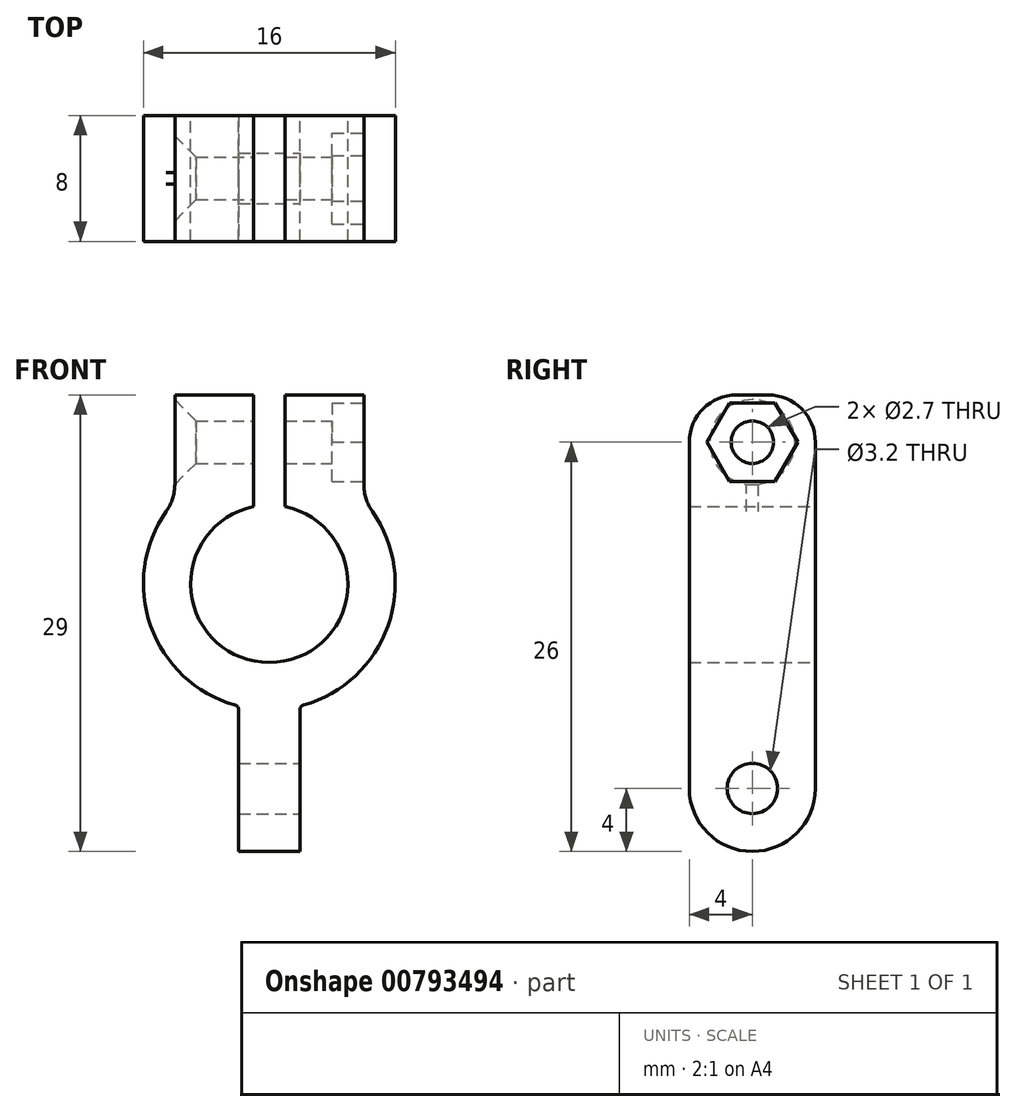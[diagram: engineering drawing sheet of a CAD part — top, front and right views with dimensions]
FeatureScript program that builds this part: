
annotation { "Feature Type Name" : "Feature", "Feature Type Description" : "" }
export const myFeature = defineFeature(function(context is Context, id is Id, definition is map)
    precondition{}
    {
        {
            var Q0;
            Q0=qCreatedBy(makeId("Front.planeOp"),FACE);
            var sketch = newSketch(context, id + "F0", { "sketchPlane" : qUnion([Q0])});
            skArc(sketch, "E0", {"start": v(-1, 4.9) * mm, "mid": v(0, -5) * mm, "end": v(1, 4.9) * mm});
            skLineSegment(sketch, "E1", {"start": v(-1, 12) * mm, "end": v(-1, 4.9) * mm});
            skLineSegment(sketch, "E2", {"start": v(1, 4.9) * mm, "end": v(1, 12) * mm});
            skLineSegment(sketch, "E3.trimOffspring", {"start": v(-1, 12) * mm, "end": v(-6, 12) * mm});
            skLineSegment(sketch, "E4", {"start": v(-1.95, -17) * mm, "end": v(-1.95, -8) * mm});
            skLineSegment(sketch, "E5", {"start": v(1.95, -8) * mm, "end": v(1.95, -17) * mm});
            skLineSegment(sketch, "E6", {"start": v(-1.95, -8) * mm, "end": v(-2.26, -8) * mm, "construction": true});
            skArc(sketch, "E7", {"start": v(-1.95, -8) * mm, "mid": v(-2.01, -7.81) * mm, "end": v(-2.18, -7.7) * mm});
            skLineSegment(sketch, "E8", {"start": v(-1.95, -17) * mm, "end": v(1.95, -17) * mm});
            skArc(sketch, "E9.MirrorCS", {"start": v(1.95, -8) * mm, "mid": v(2.01, -7.81) * mm, "end": v(2.18, -7.7) * mm});
            skLineSegment(sketch, "E10", {"start": v(-6, 12) * mm, "end": v(-6, 5.3) * mm});
            skArc(sketch, "E11", {"start": v(-2.18, -7.7) * mm, "mid": v(-7.67, -2.26) * mm, "end": v(-6, 5.3) * mm});
            skArc(sketch, "E12.MirrorCS", {"start": v(2.18, -7.7) * mm, "mid": v(7.67, -2.26) * mm, "end": v(6, 5.3) * mm});
            skLineSegment(sketch, "E13.MirrorCS", {"start": v(1, 12) * mm, "end": v(6, 12) * mm});
            skLineSegment(sketch, "E14.MirrorCS", {"start": v(6, 12) * mm, "end": v(6, 5.3) * mm});
            skSolve(sketch);
        }
        {
            var Q0;
            Q0=makeQuery(id+"F0.imprint","IMPRINT",FACE,{"disambiguationData":[TD([[makeQuery(id+"F0.imprint","IMPRINT",EDGE,{"derivedFrom":sQuery(id+"F0.wireOp",EDGE,"E0")}),-1.0]])]});
            var Q1;
            {var subQ0=sQuery(id+"F0.wireOp",EDGE,"gT4Yp9KQ-vHPQ-P8ZU-SFqX-VDEBA4EE69W3");Q1=makeQuery(id+"F0.imprint","IMPRINT",FACE,{"disambiguationData":[TD([[makeQuery(id+"F0.imprint","IMPRINT",EDGE,{"derivedFrom":subQ0}),1.0]])]});}
            extrude(context, id + "F1", {"entities" : qUnion([Q0, Q1]), "endBound" : BoundingType.SYMMETRIC, "depth" : 8 * mm, "offsetDistance" : 25 * mm});
        }
        {
            var Q0;
            Q0=makeQuery(id+"F1.opExtrude","SWEPT_FACE",FACE,{"disambiguationData":[OSD([sQuery(id+"F0.wireOp",EDGE,"E14.MirrorCS")])]});
            var sketch = newSketch(context, id + "F2", { "sketchPlane" : qUnion([Q0])});
            skCircle(sketch, "E15", {"center": v(0, 9) * mm, "radius": 1.35 * mm});
            skCircle(sketch, "E16.cCircle", {"center": v(0, 9) * mm, "radius": 2.5 * mm, "construction": true});
            skLineSegment(sketch, "E16.0", {"start": v(1.44, 11.5) * mm, "end": v(2.89, 9) * mm});
            skLineSegment(sketch, "E16.1", {"start": v(2.89, 9) * mm, "end": v(1.44, 6.5) * mm});
            skLineSegment(sketch, "E16.2", {"start": v(1.44, 6.5) * mm, "end": v(-1.44, 6.5) * mm});
            skLineSegment(sketch, "E16.3", {"start": v(-1.44, 6.5) * mm, "end": v(-2.89, 9) * mm});
            skLineSegment(sketch, "E16.4", {"start": v(-2.89, 9) * mm, "end": v(-1.44, 11.5) * mm});
            skLineSegment(sketch, "E16.5", {"start": v(-1.44, 11.5) * mm, "end": v(1.44, 11.5) * mm});
            skPoint(sketch, "E16.0.midPoint", {"position": v(2.17, 10.25) * mm});
            skSolve(sketch);
        }
        {
            var Q0;
            Q0=makeQuery(id+"F2.imprint","IMPRINT",FACE,{"disambiguationData":[TD([[makeQuery(id+"F2.imprint","IMPRINT",EDGE,{"derivedFrom":sQuery(id+"F2.wireOp",EDGE,"E15")}),1.0]])]});
            var Q1;
            {var subQ0=sQuery(id+"F2.wireOp",EDGE,"nRwaLtps-0aPM-k6Bh-PqO4-CJdIWXvHlXeP");Q1=makeQuery(id+"F2.imprint","IMPRINT",FACE,{"disambiguationData":[TD([[makeQuery(id+"F2.imprint","IMPRINT",EDGE,{"derivedFrom":subQ0}),1.0]])]});}
            var Q2;
            {var subQ0=sQuery(id+"F2.wireOp",EDGE,"26d730cf-6a02-49fb-9eb9-cb2f17dd4a160.MirrorCS");Q2=makeQuery(id+"F2.imprint","IMPRINT",FACE,{"disambiguationData":[TD([[makeQuery(id+"F2.imprint","IMPRINT",EDGE,{"derivedFrom":subQ0}),-1.0]])]});}
            extrude(context, id + "F3", {"entities" : qUnion([Q0, Q1, Q2]), "operationType" : NewBodyOperationType.REMOVE, "oppositeDirection" : true, "depth" : 25 * mm, "offsetDistance" : 25 * mm});
        }
        {
            var Q0;
            Q0=makeQuery(id+"F2.imprint","IMPRINT",FACE,{"disambiguationData":[TD([[makeQuery(id+"F2.imprint","IMPRINT",EDGE,{"derivedFrom":sQuery(id+"F2.wireOp",EDGE,"E15")}),-1.0]])]});
            extrude(context, id + "F4", {"entities" : qUnion([Q0]), "operationType" : NewBodyOperationType.REMOVE, "oppositeDirection" : true, "depth" : 2 * mm, "offsetDistance" : 25 * mm});
        }
        {
            var Q0;
            Q0=makeQuery(id+"F1.opExtrude","SWEPT_FACE",FACE,{"disambiguationData":[OSD([sQuery(id+"F0.wireOp",EDGE,"E5")])]});
            var sketch = newSketch(context, id + "F5", { "sketchPlane" : qUnion([Q0])});
            skCircle(sketch, "E17", {"center": v(0, -13) * mm, "radius": 1.6 * mm});
            skSolve(sketch);
        }
        {
            var Q0;
            Q0=makeQuery(id+"F5.imprint","IMPRINT",FACE,{"disambiguationData":[TD([[makeQuery(id+"F5.imprint","IMPRINT",EDGE,{"derivedFrom":sQuery(id+"F5.wireOp",EDGE,"E17")}),1.0]])]});
            var Q1;
            {var subQ0=sQuery(id+"F5.wireOp",EDGE,"dgfmRsRT-HZR4-KMtm-UVD4-OGYZ9sb2hiea");var subQ1=sQuery(id+"F0.wireOp",EDGE,"URoOaodK-mer2-KlBf-KcxF-PiR6j1BPeDQ6");var subQ2=makeQuery(id+"F1.opExtrude","CAP_EDGE",EDGE,{"disambiguationData":[OSD([subQ1])],"isStart":false});var subQ3=makeQuery(id+"F5.imprint","INTERSECT",VERTEX,{"derivedFrom":[subQ2,sQuery(id+"F5.wireOp",EDGE,"iwAXt04E-8AKp-sdOK-APD1-idUJ9iq6WJ0X"),subQ0]});Q1=makeQuery(id+"F5.imprint","IMPRINT",FACE,{"disambiguationData":[TD([[makeQuery(id+"F5.imprint","IMPRINT",EDGE,{"disambiguationData":[TD([[subQ3,-1.0]])],"derivedFrom":subQ0}),-1.0]])]});}
            var Q2;
            {var subQ0=sQuery(id+"F5.wireOp",EDGE,"dgfmRsRT-HZR4-KMtm-UVD4-OGYZ9sb2hiea");var subQ1=sQuery(id+"F0.wireOp",EDGE,"URoOaodK-mer2-KlBf-KcxF-PiR6j1BPeDQ6");var subQ2=makeQuery(id+"F1.opExtrude","CAP_EDGE",EDGE,{"disambiguationData":[OSD([subQ1])],"isStart":true});var subQ3=makeQuery(id+"F5.imprint","INTERSECT",VERTEX,{"derivedFrom":[subQ2,sQuery(id+"F5.wireOp",EDGE,"2524a595-133a-427d-9363-88fda697d8180.MirrorCS"),subQ0]});Q2=makeQuery(id+"F5.imprint","IMPRINT",FACE,{"disambiguationData":[TD([[makeQuery(id+"F5.imprint","IMPRINT",EDGE,{"disambiguationData":[TD([[subQ3,1.0]])],"derivedFrom":subQ0}),-1.0]])]});}
            extrude(context, id + "F6", {"entities" : qUnion([Q0, Q1, Q2]), "operationType" : NewBodyOperationType.REMOVE, "oppositeDirection" : true, "depth" : 25 * mm, "offsetDistance" : 25 * mm});
        }
        {
            var Q0;
            Q0=makeQuery(id+"F3.boolean.opBoolean","INTERSECT",EDGE,{"derivedFrom":[makeQuery(id+"F1.opExtrude","SWEPT_FACE",FACE,{"disambiguationData":[OSD([sQuery(id+"F0.wireOp",EDGE,"E10")])]}),makeQuery(id+"F3.opExtrude","SWEPT_FACE",FACE,{"disambiguationData":[OSD([sQuery(id+"F2.wireOp",EDGE,"E15")])]})]});
            chamfer(context, id + "F7", {"entities" : qUnion([Q0]), "width" : 1.35 * mm, "tangentPropagation" : true});
        }
        {
            var Q0;
            Q0=makeQuery(id+"F1.opExtrude","CAP_EDGE",EDGE,{"disambiguationData":[OSD([sQuery(id+"F0.wireOp",EDGE,"E3.trimOffspring")])],"isStart":false});
            var Q1;
            Q1=makeQuery(id+"F1.opExtrude","CAP_EDGE",EDGE,{"disambiguationData":[OSD([sQuery(id+"F0.wireOp",EDGE,"E3.trimOffspring")])],"isStart":true});
            var Q2;
            Q2=makeQuery(id+"F1.opExtrude","CAP_EDGE",EDGE,{"disambiguationData":[OSD([sQuery(id+"F0.wireOp",EDGE,"E13.MirrorCS")])],"isStart":true});
            var Q3;
            Q3=makeQuery(id+"F1.opExtrude","CAP_EDGE",EDGE,{"disambiguationData":[OSD([sQuery(id+"F0.wireOp",EDGE,"E13.MirrorCS")])],"isStart":false});
            var Q4;
            Q4=makeQuery(id+"F1.opExtrude","SWEPT_EDGE",EDGE,{"disambiguationData":[OSD([sQuery(id+"F0.wireOp",EDGE,"E12.MirrorCS"),sQuery(id+"F0.wireOp",EDGE,"E14.MirrorCS")])]});
            var Q5;
            Q5=makeQuery(id+"F1.opExtrude","SWEPT_EDGE",EDGE,{"disambiguationData":[OSD([sQuery(id+"F0.wireOp",EDGE,"E10"),sQuery(id+"F0.wireOp",EDGE,"E11")])]});
            fillet(context, id + "F8", {"entities" : qUnion([Q0, Q1, Q2, Q3, Q4, Q5]), "radius" : 3 * mm, "tangentPropagation" : true, "allowEdgeOverflow" : false});
        }
        {
            var Q0;
            Q0=makeQuery(id+"F1.opExtrude","CAP_EDGE",EDGE,{"disambiguationData":[OSD([sQuery(id+"F0.wireOp",EDGE,"E8")])],"isStart":false});
            var Q1;
            Q1=makeQuery(id+"F1.opExtrude","CAP_EDGE",EDGE,{"disambiguationData":[OSD([sQuery(id+"F0.wireOp",EDGE,"E8")])],"isStart":true});
            fillet(context, id + "F9", {"entities" : qUnion([Q0, Q1]), "radius" : 4 * mm, "tangentPropagation" : true, "allowEdgeOverflow" : false});
        }
    });
